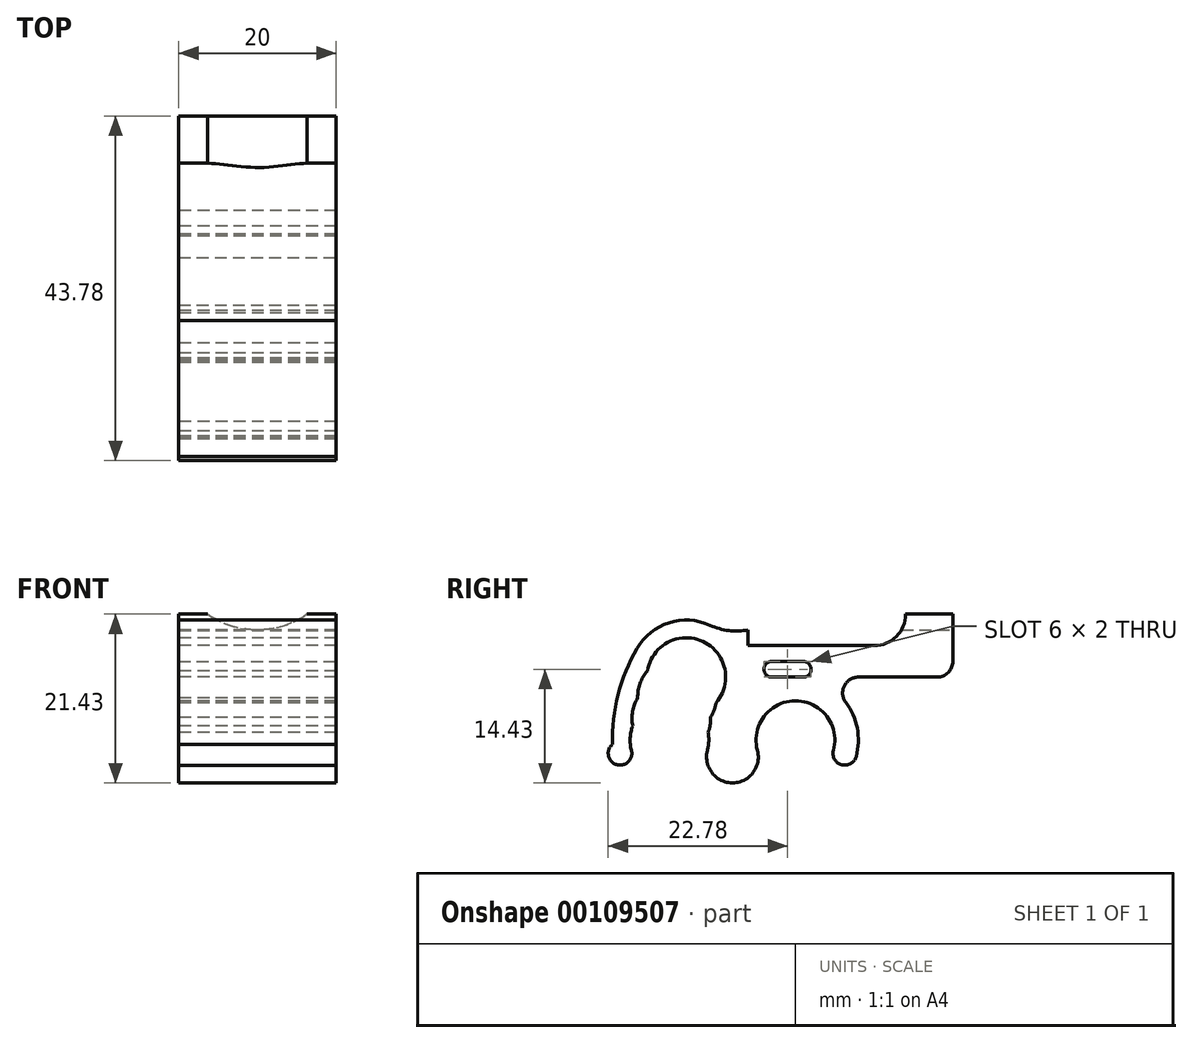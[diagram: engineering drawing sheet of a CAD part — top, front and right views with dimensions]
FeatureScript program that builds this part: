
annotation { "Feature Type Name" : "Feature", "Feature Type Description" : "" }
export const myFeature = defineFeature(function(context is Context, id is Id, definition is map)
    precondition{}
    {
        {
            var Q0;
            Q0=qCreatedBy(makeId("Right.planeOp"),FACE);
            var sketch = newSketch(context, id + "F0", { "sketchPlane" : qUnion([Q0])});
            skCircle(sketch, "E0", {"center": v(0, 0) * mm, "radius": 3.97 * mm, "construction": true});
            skCircle(sketch, "E1", {"center": v(-16, 0) * mm, "radius": 3.97 * mm, "construction": true});
            skCircle(sketch, "E2", {"center": v(0, 0) * mm, "radius": 16 * mm, "construction": true});
            skLineSegment(sketch, "E3", {"start": v(0, 0) * mm, "end": v(-13.86, 8) * mm, "construction": true});
            skLineSegment(sketch, "E4", {"start": v(0, 0) * mm, "end": v(-15.04, 5.47) * mm, "construction": true});
            skLineSegment(sketch, "E5", {"start": v(0, 0) * mm, "end": v(-15.76, 2.78) * mm, "construction": true});
            skArc(sketch, "E6", {"start": v(-20.66, 1.8) * mm, "mid": v(-21, 0.27) * mm, "end": v(-20.83, -1.3) * mm});
            skArc(sketch, "E7", {"start": v(-20.03, 5.37) * mm, "mid": v(-20.68, 3.65) * mm, "end": v(-20.66, 1.8) * mm});
            skArc(sketch, "E8", {"start": v(-18.8, 8.77) * mm, "mid": v(-19.73, 7.18) * mm, "end": v(-20.03, 5.37) * mm});
            skArc(sketch, "E9", {"start": v(4.83, -1.3) * mm, "mid": v(0, 5) * mm, "end": v(-4.83, -1.3) * mm});
            skArc(sketch, "E10.trimOffspring", {"start": v(-10.1, 4.7) * mm, "mid": v(-11.74, 12.53) * mm, "end": v(-18.8, 8.77) * mm});
            skArc(sketch, "E11.trimOffspring", {"start": v(-10.76, 2.88) * mm, "mid": v(-10.34, 3.76) * mm, "end": v(-10.1, 4.7) * mm});
            skArc(sketch, "E12.trimOffspring", {"start": v(-11.1, 0.97) * mm, "mid": v(-10.83, 1.91) * mm, "end": v(-10.76, 2.88) * mm});
            skLineSegment(sketch, "E13", {"start": v(-16, 0) * mm, "end": v(-25.66, -2.59) * mm, "construction": true});
            skLineSegment(sketch, "E14", {"start": v(-16, 0) * mm, "end": v(-6.34, -2.59) * mm, "construction": true});
            skArc(sketch, "E15", {"start": v(7.73, -2.07) * mm, "mid": v(7.85, 1.52) * mm, "end": v(6.4, 4.8) * mm});
            skArc(sketch, "E16", {"start": v(-20.14, 11.62) * mm, "mid": v(-22.53, 5.76) * mm, "end": v(-23.24, -0.53) * mm});
            skPoint(sketch, "E17.start.orphan", {"position": v(0, -8) * mm});
            skArc(sketch, "E18.trimOffspring", {"start": v(-10.83, 14.59) * mm, "mid": v(-16.06, 14.9) * mm, "end": v(-20.14, 11.62) * mm});
            skArc(sketch, "E19", {"start": v(-23.24, -0.53) * mm, "mid": v(-22.73, -3.11) * mm, "end": v(-20.83, -1.3) * mm});
            skArc(sketch, "E20.trimOffspring", {"start": v(-11.17, -1.3) * mm, "mid": v(-11, -0.17) * mm, "end": v(-11.1, 0.97) * mm});
            skArc(sketch, "E21", {"start": v(-11.17, -1.3) * mm, "mid": v(-8, -5.43) * mm, "end": v(-4.83, -1.3) * mm});
            skLineSegment(sketch, "E22", {"start": v(-4.83, -1.3) * mm, "end": v(4.83, -1.3) * mm, "construction": true});
            skArc(sketch, "E23", {"start": v(4.83, -1.3) * mm, "mid": v(5.9, -3.13) * mm, "end": v(7.73, -2.07) * mm});
            skLineSegment(sketch, "E24", {"start": v(0, 0) * mm, "end": v(0, 16) * mm, "construction": true});
            skLineSegment(sketch, "E25", {"start": v(-6, 12) * mm, "end": v(-6, 14) * mm});
            skLineSegment(sketch, "E26", {"start": v(-6, 12) * mm, "end": v(10, 12) * mm});
            skLineSegment(sketch, "E27", {"start": v(20, 16) * mm, "end": v(14, 16) * mm});
            skLineSegment(sketch, "E28", {"start": v(20, 16) * mm, "end": v(20, 10) * mm});
            skArc(sketch, "E29", {"start": v(-10.83, 14.59) * mm, "mid": v(-8.46, 13.92) * mm, "end": v(-6, 14) * mm});
            skArc(sketch, "E30", {"start": v(10, 12) * mm, "mid": v(12.83, 13.17) * mm, "end": v(14, 16) * mm});
            skLineSegment(sketch, "E31", {"start": v(18, 8) * mm, "end": v(8, 8) * mm});
            skPoint(sketch, "E32.visualSharp", {"position": v(20, 8) * mm});
            skArc(sketch, "E32.filletArc", {"start": v(18, 8) * mm, "mid": v(19.41, 8.59) * mm, "end": v(20, 10) * mm});
            skArc(sketch, "E33", {"start": v(8, 8) * mm, "mid": v(6.21, 6.9) * mm, "end": v(6.4, 4.8) * mm});
            skSolve(sketch);
        }
        {
            var Q0;
            Q0=qSketchRegion(id+"F0",true);
            extrude(context, id + "F1", {"entities" : qUnion([Q0]), "endBound" : BoundingType.SYMMETRIC, "depth" : 20 * mm});
        }
        {
            var Q0;
            Q0=makeQuery(id+"F1.opExtrude","CAP_FACE",FACE,{"disambiguationData":[OSD([sQuery(id+"F0.wireOp",EDGE,"E6"),sQuery(id+"F0.wireOp",EDGE,"E7"),sQuery(id+"F0.wireOp",EDGE,"E8"),sQuery(id+"F0.wireOp",EDGE,"E9"),sQuery(id+"F0.wireOp",EDGE,"E10.trimOffspring"),sQuery(id+"F0.wireOp",EDGE,"E11.trimOffspring"),sQuery(id+"F0.wireOp",EDGE,"E12.trimOffspring"),sQuery(id+"F0.wireOp",EDGE,"E15"),sQuery(id+"F0.wireOp",EDGE,"E16"),sQuery(id+"F0.wireOp",EDGE,"E18.trimOffspring"),sQuery(id+"F0.wireOp",EDGE,"E19"),sQuery(id+"F0.wireOp",EDGE,"E20.trimOffspring"),sQuery(id+"F0.wireOp",EDGE,"E21"),sQuery(id+"F0.wireOp",EDGE,"E23"),sQuery(id+"F0.wireOp",EDGE,"E25"),sQuery(id+"F0.wireOp",EDGE,"E26"),sQuery(id+"F0.wireOp",EDGE,"E27"),sQuery(id+"F0.wireOp",EDGE,"E28"),sQuery(id+"F0.wireOp",EDGE,"E29"),sQuery(id+"F0.wireOp",EDGE,"E30"),sQuery(id+"F0.wireOp",EDGE,"E31"),sQuery(id+"F0.wireOp",EDGE,"E32.filletArc"),sQuery(id+"F0.wireOp",EDGE,"E33")])],"isStart":false});
            var sketch = newSketch(context, id + "F2", { "sketchPlane" : qUnion([Q0])});
            skLineSegment(sketch, "E34", {"start": v(-3, 10) * mm, "end": v(1, 10) * mm});
            skLineSegment(sketch, "E35", {"start": v(-3, 8) * mm, "end": v(1, 8) * mm});
            skArc(sketch, "E36", {"start": v(-3, 10) * mm, "mid": v(-4, 9) * mm, "end": v(-3, 8) * mm});
            skArc(sketch, "E37", {"start": v(1, 8) * mm, "mid": v(2, 9) * mm, "end": v(1, 10) * mm});
            skSolve(sketch);
        }
        {
            var Q0;
            Q0=qSketchRegion(id+"F2",true);
            var Q1;
            Q1=makeQuery(id+"F1.opExtrude","CAP_FACE",FACE,{"disambiguationData":[OSD([sQuery(id+"F0.wireOp",EDGE,"E6"),sQuery(id+"F0.wireOp",EDGE,"E7"),sQuery(id+"F0.wireOp",EDGE,"E8"),sQuery(id+"F0.wireOp",EDGE,"E9"),sQuery(id+"F0.wireOp",EDGE,"E10.trimOffspring"),sQuery(id+"F0.wireOp",EDGE,"E11.trimOffspring"),sQuery(id+"F0.wireOp",EDGE,"E12.trimOffspring"),sQuery(id+"F0.wireOp",EDGE,"E15"),sQuery(id+"F0.wireOp",EDGE,"E16"),sQuery(id+"F0.wireOp",EDGE,"E18.trimOffspring"),sQuery(id+"F0.wireOp",EDGE,"E19"),sQuery(id+"F0.wireOp",EDGE,"E20.trimOffspring"),sQuery(id+"F0.wireOp",EDGE,"E21"),sQuery(id+"F0.wireOp",EDGE,"E23"),sQuery(id+"F0.wireOp",EDGE,"E25"),sQuery(id+"F0.wireOp",EDGE,"E26"),sQuery(id+"F0.wireOp",EDGE,"E27"),sQuery(id+"F0.wireOp",EDGE,"E28"),sQuery(id+"F0.wireOp",EDGE,"E29"),sQuery(id+"F0.wireOp",EDGE,"E30"),sQuery(id+"F0.wireOp",EDGE,"E31"),sQuery(id+"F0.wireOp",EDGE,"E32.filletArc"),sQuery(id+"F0.wireOp",EDGE,"E33")])],"isStart":true});
            extrude(context, id + "F3", {"entities" : qUnion([Q0]), "operationType" : NewBodyOperationType.REMOVE, "endBound" : BoundingType.UP_TO_SURFACE, "oppositeDirection" : true, "endBoundEntityFace" : qUnion([Q1]), "depth" : 25 * mm});
        }
        {
            var Q0;
            Q0=makeQuery(id+"F1.opExtrude","SWEPT_FACE",FACE,{"disambiguationData":[OSD([sQuery(id+"F0.wireOp",EDGE,"E28")])]});
            var sketch = newSketch(context, id + "F4", { "sketchPlane" : qUnion([Q0])});
            skLineSegment(sketch, "E38", {"start": v(0, 10) * mm, "end": v(0, 25) * mm, "construction": true});
            skPoint(sketch, "E38.endSnap0", {"position": v(0, 10) * mm});
            skArc(sketch, "E39", {"start": v(-6.32, 16) * mm, "mid": v(0, 14) * mm, "end": v(6.32, 16) * mm});
            skLineSegment(sketch, "E40", {"start": v(-6.32, 16) * mm, "end": v(6.32, 16) * mm});
            skSolve(sketch);
        }
        {
            var Q0;
            Q0=qSketchRegion(id+"F4",true);
            var Q1;
            Q1=makeQuery(id+"F1.opExtrude","SWEPT_FACE",FACE,{"disambiguationData":[OSD([sQuery(id+"F0.wireOp",EDGE,"E30")])]});
            extrude(context, id + "F5", {"entities" : qUnion([Q0]), "operationType" : NewBodyOperationType.REMOVE, "endBound" : BoundingType.UP_TO_SURFACE, "oppositeDirection" : true, "endBoundEntityFace" : qUnion([Q1]), "depth" : 25 * mm});
        }
    });
